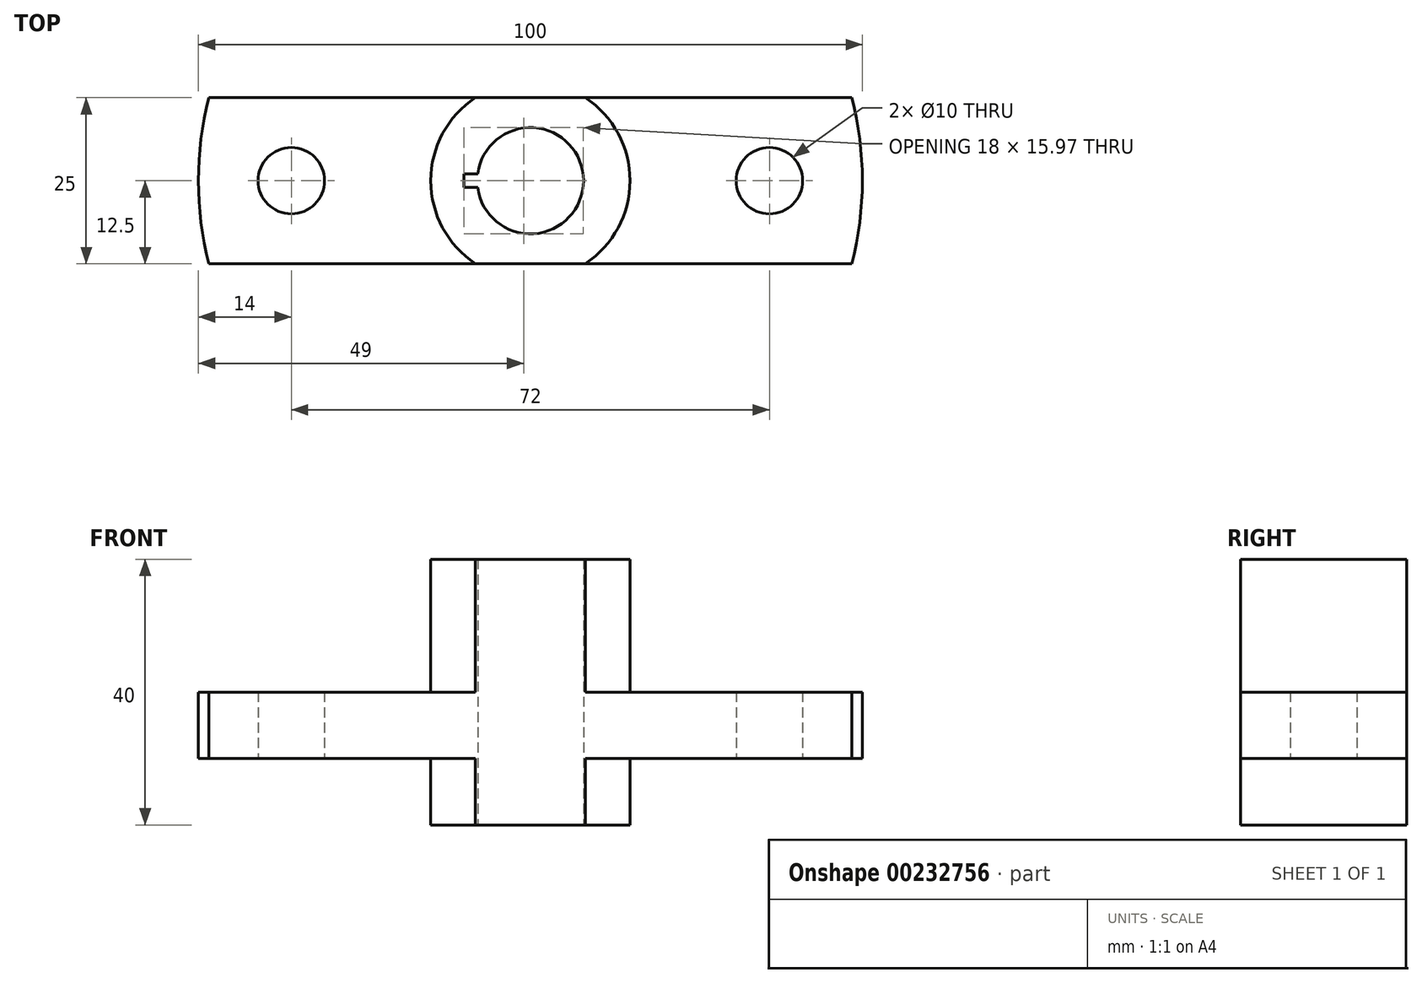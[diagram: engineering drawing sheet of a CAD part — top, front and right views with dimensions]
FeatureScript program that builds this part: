
annotation { "Feature Type Name" : "Feature", "Feature Type Description" : "" }
export const myFeature = defineFeature(function(context is Context, id is Id, definition is map)
    precondition{}
    {
        {
            var Q0;
            Q0=qCreatedBy(makeId("Top.planeOp"),FACE);
            var sketch = newSketch(context, id + "F0", { "sketchPlane" : qUnion([Q0])});
            skArc(sketch, "E0", {"start": v(-7.94, -1) * mm, "mid": v(8, 0) * mm, "end": v(-7.94, 1) * mm});
            skArc(sketch, "E1", {"start": v(-8.3, 12.5) * mm, "mid": v(-15, 0) * mm, "end": v(-8.3, -12.5) * mm});
            skLineSegment(sketch, "E2", {"start": v(-36.25, 0) * mm, "end": v(40.45, 0) * mm, "construction": true});
            skLineSegment(sketch, "E3.bottom", {"start": v(-10, 1) * mm, "end": v(-7.94, 1) * mm});
            skLineSegment(sketch, "E3.top", {"start": v(-10, -1) * mm, "end": v(-7.94, -1) * mm});
            skLineSegment(sketch, "E3.left", {"start": v(-10, 1) * mm, "end": v(-10, -1) * mm});
            skArc(sketch, "E4", {"start": v(-48.41, 12.5) * mm, "mid": v(-50, 0) * mm, "end": v(-48.41, -12.5) * mm});
            skLineSegment(sketch, "E5.bottom", {"start": v(-48.41, 12.5) * mm, "end": v(48.41, 12.5) * mm});
            skLineSegment(sketch, "E5.top", {"start": v(-48.41, -12.5) * mm, "end": v(48.41, -12.5) * mm});
            skArc(sketch, "E6.trimOffspring", {"start": v(48.41, -12.5) * mm, "mid": v(50, 0) * mm, "end": v(48.41, 12.5) * mm});
            skArc(sketch, "E7.trimOffspring", {"start": v(8.3, -12.5) * mm, "mid": v(15, 0) * mm, "end": v(8.3, 12.5) * mm});
            skSolve(sketch);
        }
        {
            var Q0;
            Q0=makeQuery(id+"F0.imprint","IMPRINT",FACE,{"disambiguationData":[TD([[makeQuery(id+"F0.imprint","IMPRINT",EDGE,{"derivedFrom":sQuery(id+"F0.wireOp",EDGE,"E0")}),-1.0]])]});
            extrude(context, id + "F1", {"entities" : qUnion([Q0]), "depth" : 40 * mm});
        }
        {
            var Q0;
            Q0=qCreatedBy(makeId("Top.planeOp"),FACE);
            cPlane(context, id + "F2", {"entities" : qUnion([Q0]), "cplaneType" : CPlaneType.OFFSET, "offset" : 10 * mm, "width" : 150 * mm, "height" : 150 * mm});
        }
        {
            var Q0;
            Q0=qCreatedBy(id+"F2.planeOp",FACE);
            var sketch = newSketch(context, id + "F3", { "sketchPlane" : qUnion([Q0])});
            skArc(sketch, "E8.0", {"start": v(-7.94, -1) * mm, "mid": v(8, 0) * mm, "end": v(-7.94, 1) * mm});
            skArc(sketch, "E8.1", {"start": v(-8.3, 12.5) * mm, "mid": v(-15, 0) * mm, "end": v(-8.3, -12.5) * mm});
            skLineSegment(sketch, "E8.2", {"start": v(-36.25, 0) * mm, "end": v(40.45, 0) * mm, "construction": true});
            skLineSegment(sketch, "E8.3", {"start": v(-10, 1) * mm, "end": v(-7.94, 1) * mm});
            skLineSegment(sketch, "E8.4", {"start": v(-10, -1) * mm, "end": v(-7.94, -1) * mm});
            skLineSegment(sketch, "E8.5", {"start": v(-10, 1) * mm, "end": v(-10, -1) * mm});
            skArc(sketch, "E8.6", {"start": v(-48.41, 12.5) * mm, "mid": v(-50, 0) * mm, "end": v(-48.41, -12.5) * mm});
            skLineSegment(sketch, "E8.7", {"start": v(-48.41, 12.5) * mm, "end": v(48.41, 12.5) * mm});
            skLineSegment(sketch, "E8.8", {"start": v(-48.41, -12.5) * mm, "end": v(48.41, -12.5) * mm});
            skArc(sketch, "E8.9", {"start": v(48.41, -12.5) * mm, "mid": v(50, 0) * mm, "end": v(48.41, 12.5) * mm});
            skArc(sketch, "E8.10", {"start": v(8.3, -12.5) * mm, "mid": v(15, 0) * mm, "end": v(8.3, 12.5) * mm});
            skCircle(sketch, "E9", {"center": v(-36, 0) * mm, "radius": 5 * mm});
            skCircle(sketch, "E10", {"center": v(36, 0) * mm, "radius": 5 * mm});
            skSolve(sketch);
        }
        {
            var Q0;
            {var subQ1=sQuery(id+"F3.wireOp",EDGE,"E8.1");Q0=makeQuery(id+"F3.imprint","IMPRINT",FACE,{"disambiguationData":[TD([[makeQuery(id+"F3.imprint","IMPRINT",EDGE,{"derivedFrom":subQ1}),-1.0]])]});}
            var Q1;
            {var subQ1=sQuery(id+"F3.wireOp",EDGE,"E8.9");Q1=makeQuery(id+"F3.imprint","IMPRINT",FACE,{"disambiguationData":[TD([[makeQuery(id+"F3.imprint","IMPRINT",EDGE,{"derivedFrom":subQ1}),1.0]])]});}
            extrude(context, id + "F4", {"entities" : qUnion([Q0, Q1]), "operationType" : NewBodyOperationType.ADD, "depth" : 10 * mm});
        }
    });
